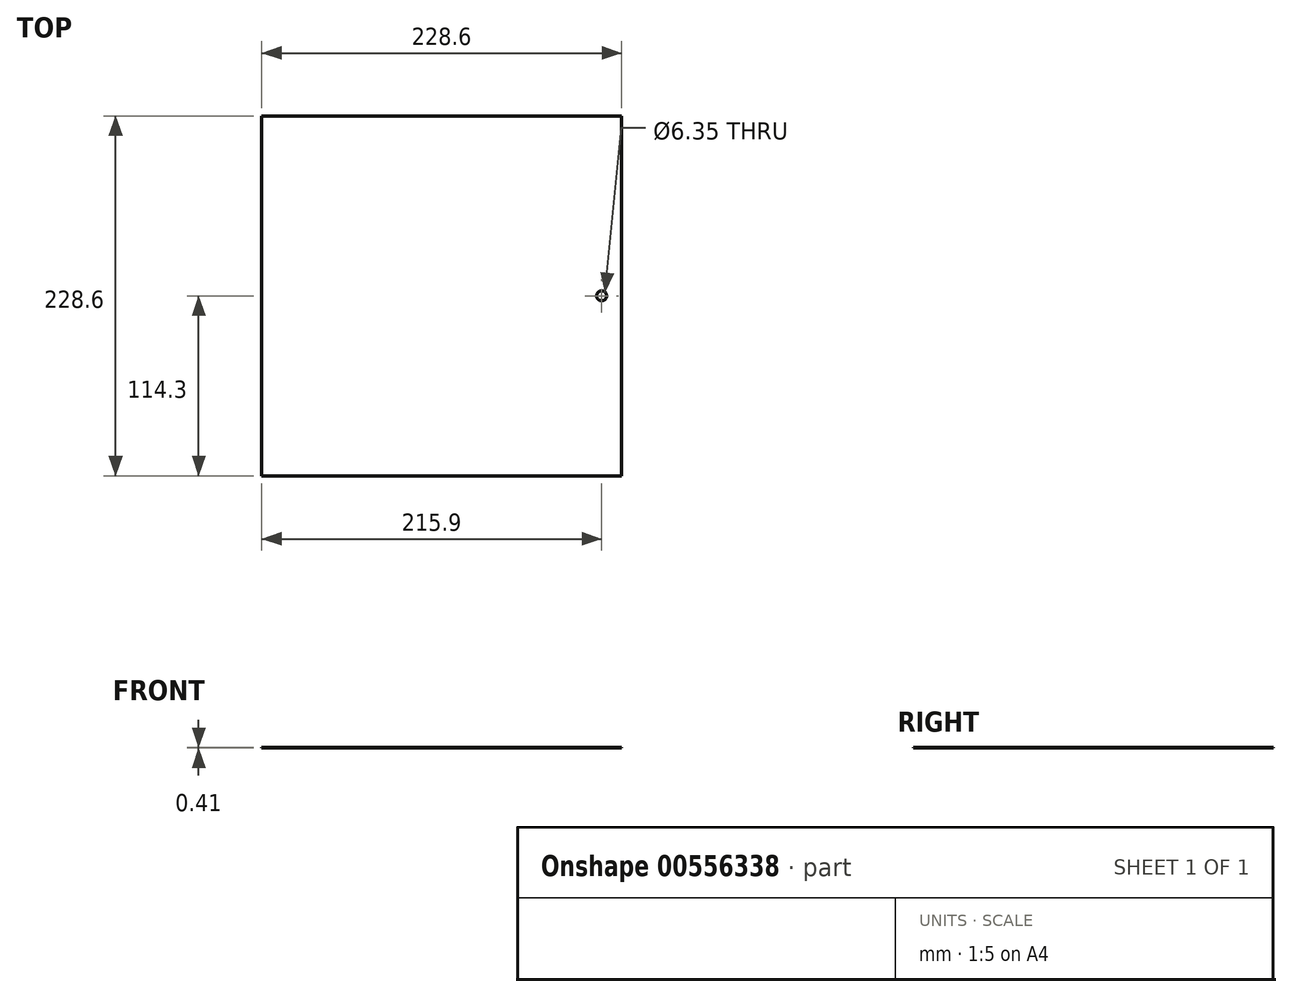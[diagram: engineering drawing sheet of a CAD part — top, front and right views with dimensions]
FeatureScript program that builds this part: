
annotation { "Feature Type Name" : "Feature", "Feature Type Description" : "" }
export const myFeature = defineFeature(function(context is Context, id is Id, definition is map)
    precondition{}
    {
        {
            var Q0;
            Q0=qCreatedBy(makeId("Top.planeOp"),FACE);
            var sketch = newSketch(context, id + "F0", { "sketchPlane" : qUnion([Q0])});
            skLineSegment(sketch, "E0.bottom", {"start": v(0, 0) * mm, "end": v(-228.6, 0) * mm});
            skLineSegment(sketch, "E0.top", {"start": v(0, -228.6) * mm, "end": v(-228.6, -228.6) * mm});
            skLineSegment(sketch, "E0.left", {"start": v(0, 0) * mm, "end": v(0, -228.6) * mm});
            skLineSegment(sketch, "E0.right", {"start": v(-228.6, 0) * mm, "end": v(-228.6, -228.6) * mm});
            skSolve(sketch);
        }
        {
            var Q0;
            Q0=makeQuery(id+"F0.imprint","IMPRINT",FACE,{"disambiguationData":[TD([[makeQuery(id+"F0.imprint","IMPRINT",EDGE,{"derivedFrom":sQuery(id+"F0.wireOp",EDGE,"E0.bottom")}),1.0]])]});
            extrude(context, id + "F1", {"entities" : qUnion([Q0]), "depth" : 0.4 * mm, "offsetDistance" : 25.4 * mm});
        }
        {
            var Q0;
            Q0=makeQuery(id+"F1.opExtrude","CAP_FACE",FACE,{"disambiguationData":[OSD([sQuery(id+"F0.wireOp",EDGE,"E0.bottom"),sQuery(id+"F0.wireOp",EDGE,"E0.top"),sQuery(id+"F0.wireOp",EDGE,"E0.left"),sQuery(id+"F0.wireOp",EDGE,"E0.right")])],"isStart":false});
            var sketch = newSketch(context, id + "F2", { "sketchPlane" : qUnion([Q0])});
            skCircle(sketch, "E1", {"center": v(-12.7, -114.3) * mm, "radius": 3.18 * mm});
            skSolve(sketch);
        }
        {
            var Q0;
            Q0=makeQuery(id+"F2.imprint","IMPRINT",FACE,{"disambiguationData":[TD([[makeQuery(id+"F2.imprint","IMPRINT",EDGE,{"derivedFrom":sQuery(id+"F2.wireOp",EDGE,"E1")}),1.0]])]});
            extrude(context, id + "F3", {"entities" : qUnion([Q0]), "operationType" : NewBodyOperationType.REMOVE, "endBound" : BoundingType.THROUGH_ALL, "oppositeDirection" : true, "depth" : 25.4 * mm, "offsetDistance" : 25.4 * mm});
        }
    });
